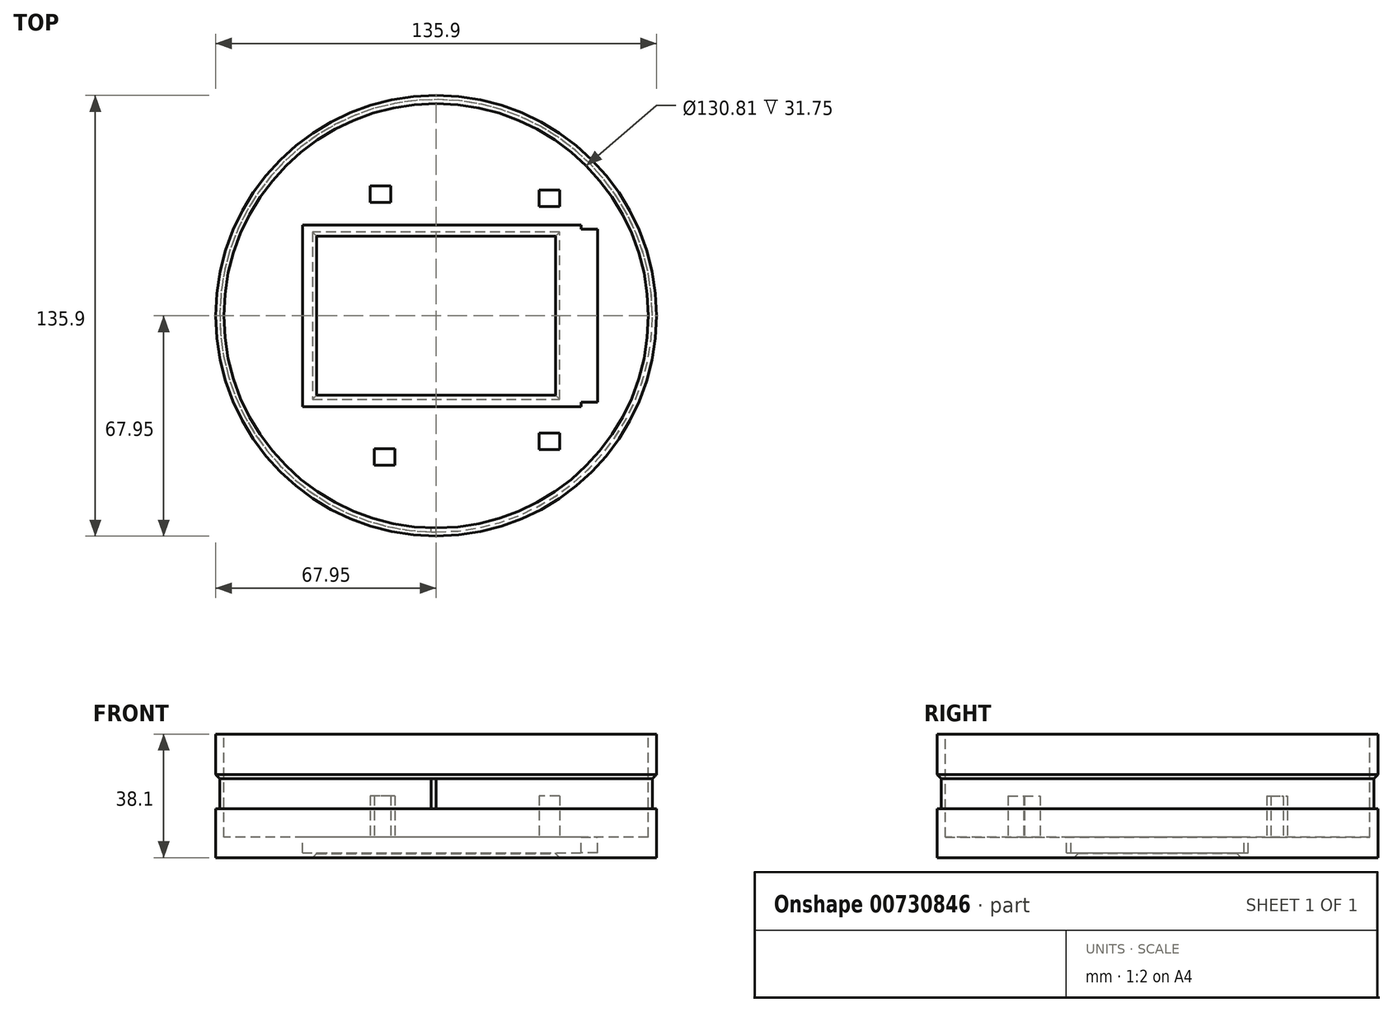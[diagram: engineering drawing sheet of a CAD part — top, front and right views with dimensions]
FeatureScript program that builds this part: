
annotation { "Feature Type Name" : "Feature", "Feature Type Description" : "" }
export const myFeature = defineFeature(function(context is Context, id is Id, definition is map)
    precondition{}
    {
        {
            var Q0;
            Q0=qCreatedBy(makeId("Top.planeOp"),FACE);
            var sketch = newSketch(context, id + "F0", { "sketchPlane" : qUnion([Q0])});
            skCircle(sketch, "E0", {"center": v(0, 0) * mm, "radius": 67.95 * mm});
            skSolve(sketch);
        }
        {
            var Q0;
            Q0 = qSketchRegion(id + "F0", true);
            extrude(context, id + "F1", {"entities" : qUnion([Q0]), "oppositeDirection" : true, "depth" : 38.1 * mm, "offsetDistance" : 25.4 * mm});
        }
        {
            var Q0;
            Q0=makeQuery(id+"F1.opExtrude","CAP_FACE",FACE,{"disambiguationData":[OSD([sQuery(id+"F0.wireOp",EDGE,"E0")])],"isStart":true});
            var sketch = newSketch(context, id + "F2", { "sketchPlane" : qUnion([Q0])});
            skCircle(sketch, "E1", {"center": v(0, 0) * mm, "radius": 65.4 * mm});
            skSolve(sketch);
        }
        {
            var Q0;
            Q0 = qSketchRegion(id + "F2", true);
            extrude(context, id + "F3", {"entities" : qUnion([Q0]), "operationType" : NewBodyOperationType.REMOVE, "oppositeDirection" : true, "depth" : 31.75 * mm, "offsetDistance" : 25.4 * mm});
        }
        {
            var Q0;
            Q0=makeQuery(id+"F1.opExtrude","CAP_FACE",FACE,{"disambiguationData":[OSD([sQuery(id+"F0.wireOp",EDGE,"E0")])],"isStart":true});
            cPlane(context, id + "F4", {"entities" : qUnion([Q0]), "cplaneType" : CPlaneType.OFFSET, "offset" : 19.05 * mm, "oppositeDirection" : true, "width" : 152.4 * mm, "height" : 152.4 * mm});
        }
        {
            var Q0;
            Q0=qCreatedBy(makeId("Front.planeOp"),FACE);
            var sketch = newSketch(context, id + "F5", { "sketchPlane" : qUnion([Q0])});
            skLineSegment(sketch, "E2.bottom", {"start": v(-66.68, -15.05) * mm, "end": v(-69.22, -15.05) * mm});
            skLineSegment(sketch, "E2.top", {"start": v(-66.68, -23.05) * mm, "end": v(-69.22, -23.05) * mm});
            skLineSegment(sketch, "E2.left", {"start": v(-66.68, -15.05) * mm, "end": v(-66.68, -23.05) * mm});
            skLineSegment(sketch, "E2.right", {"start": v(-69.22, -15.05) * mm, "end": v(-69.22, -23.05) * mm});
            skPoint(sketch, "E2.middle", {"position": v(-67.95, -19.05) * mm});
            skLineSegment(sketch, "E3", {"start": v(-67.95, -13.75) * mm, "end": v(-67.95, -24.76) * mm, "construction": true});
            skSolve(sketch);
        }
        {
            var Q0;
            Q0 = qSketchRegion(id + "F5", true);
            var Q1;
            Q1=makeQuery(id+"F1.opExtrude","SWEPT_FACE",FACE,{"disambiguationData":[OSD([sQuery(id+"F0.wireOp",EDGE,"E0")])]});
            revolve(context, id + "F6", {"operationType" : NewBodyOperationType.REMOVE, "surfaceOperationType" : NewSurfaceOperationType.NEW, "entities" : qUnion([Q0]), "axis" : qUnion([Q1]), "revolveType" : RevolveType.ONE_DIRECTION, "oppositeDirection" : true, "angle" : 360 * degree});
        }
        {
            var Q0;
            Q0=makeQuery(id+"F6.boolean.opBoolean","INTERSECT",EDGE,{"derivedFrom":[makeQuery(id+"F1.opExtrude","SWEPT_FACE",FACE,{"disambiguationData":[OSD([sQuery(id+"F0.wireOp",EDGE,"E0")])]}),makeQuery(id+"F6.opRevolve","SWEPT_FACE",FACE,{"disambiguationData":[OSD([sQuery(id+"F5.wireOp",EDGE,"E2.bottom")])]})]});
            chamfer(context, id + "F7", {"entities" : qUnion([Q0]), "width" : 2.54 * mm});
        }
        {
            var Q0;
            Q0=makeQuery(id+"F3.boolean.opBoolean","COPY",FACE,{"derivedFrom":makeQuery(id+"F3.opExtrude","CAP_FACE",FACE,{"disambiguationData":[OSD([sQuery(id+"F2.wireOp",EDGE,"E1")])],"isStart":false})});
            var sketch = newSketch(context, id + "F8", { "sketchPlane" : qUnion([Q0])});
            skLineSegment(sketch, "E4.bottom", {"start": v(36.83, 24.51) * mm, "end": v(-36.83, 24.51) * mm});
            skLineSegment(sketch, "E4.top", {"start": v(36.83, -24.51) * mm, "end": v(-36.83, -24.51) * mm});
            skLineSegment(sketch, "E4.left", {"start": v(36.83, 24.51) * mm, "end": v(36.83, -24.51) * mm});
            skLineSegment(sketch, "E4.right", {"start": v(-36.83, 24.51) * mm, "end": v(-36.83, -24.51) * mm});
            skPoint(sketch, "E4.middle", {"position": v(0, 0) * mm});
            skSolve(sketch);
        }
        {
            var Q0;
            Q0 = qSketchRegion(id + "F8", true);
            extrude(context, id + "F9", {"entities" : qUnion([Q0]), "operationType" : NewBodyOperationType.REMOVE, "endBound" : BoundingType.THROUGH_ALL, "oppositeDirection" : true, "depth" : 25.4 * mm, "offsetDistance" : 25.4 * mm});
        }
        {
            var Q0;
            Q0=makeQuery(id+"F3.boolean.opBoolean","COPY",FACE,{"derivedFrom":makeQuery(id+"F3.opExtrude","CAP_FACE",FACE,{"disambiguationData":[OSD([sQuery(id+"F2.wireOp",EDGE,"E1")])],"isStart":false})});
            var sketch = newSketch(context, id + "F10", { "sketchPlane" : qUnion([Q0])});
            skLineSegment(sketch, "E5", {"start": v(1.75, 4.14) * mm, "end": v(1.75, -15.67) * mm, "construction": true});
            skLineSegment(sketch, "E6", {"start": v(-9.6, 0) * mm, "end": v(14.27, 0) * mm, "construction": true});
            skLineSegment(sketch, "E7.bottom", {"start": v(44.68, 28) * mm, "end": v(-41.18, 28) * mm});
            skLineSegment(sketch, "E7.top", {"start": v(44.68, -28) * mm, "end": v(-41.18, -28) * mm});
            skLineSegment(sketch, "E7.left", {"start": v(44.68, 28) * mm, "end": v(44.68, -28) * mm});
            skLineSegment(sketch, "E7.right", {"start": v(-41.18, 28) * mm, "end": v(-41.18, -28) * mm});
            skPoint(sketch, "E7.middle", {"position": v(1.75, 0) * mm});
            skSolve(sketch);
        }
        {
            var Q0;
            Q0 = qSketchRegion(id + "F10", true);
            var Q1;
            Q1=makeQuery(id+"F1.opExtrude","CAP_FACE",FACE,{"disambiguationData":[OSD([sQuery(id+"F0.wireOp",EDGE,"E0")])],"isStart":false});
            extrude(context, id + "F11", {"entities" : qUnion([Q0]), "operationType" : NewBodyOperationType.REMOVE, "endBound" : BoundingType.UP_TO_SURFACE, "oppositeDirection" : true, "depth" : 25.4 * mm, "endBoundEntityFace" : qUnion([Q1]), "hasOffset" : true, "offsetDistance" : 1.52 * mm});
        }
        {
            var Q0;
            Q0=makeQuery(id+"F3.boolean.opBoolean","COPY",FACE,{"derivedFrom":makeQuery(id+"F3.opExtrude","CAP_FACE",FACE,{"disambiguationData":[OSD([sQuery(id+"F2.wireOp",EDGE,"E1")])],"isStart":false})});
            var sketch = newSketch(context, id + "F12", { "sketchPlane" : qUnion([Q0])});
            skLineSegment(sketch, "E8.bottom", {"start": v(44.68, 26.67) * mm, "end": v(49.76, 26.67) * mm});
            skLineSegment(sketch, "E8.top", {"start": v(44.68, -26.67) * mm, "end": v(49.76, -26.67) * mm});
            skLineSegment(sketch, "E8.left", {"start": v(44.68, 26.67) * mm, "end": v(44.68, -26.67) * mm});
            skLineSegment(sketch, "E8.right", {"start": v(49.76, 26.67) * mm, "end": v(49.76, -26.67) * mm});
            skSolve(sketch);
        }
        {
            var Q0;
            Q0 = qSketchRegion(id + "F12", true);
            var Q1;
            Q1=makeQuery(id+"F11.boolean.opBoolean","COPY",FACE,{"derivedFrom":makeQuery(id+"F11.opExtrude","CAP_FACE",FACE,{"disambiguationData":[OSD([sQuery(id+"F10.wireOp",EDGE,"E7.bottom"),sQuery(id+"F10.wireOp",EDGE,"E7.top"),sQuery(id+"F10.wireOp",EDGE,"E7.left"),sQuery(id+"F10.wireOp",EDGE,"E7.right")])],"isStart":false})});
            extrude(context, id + "F13", {"entities" : qUnion([Q0]), "operationType" : NewBodyOperationType.REMOVE, "endBound" : BoundingType.UP_TO_SURFACE, "oppositeDirection" : true, "depth" : 3.8 * mm, "endBoundEntityFace" : qUnion([Q1]), "offsetDistance" : 25.4 * mm});
        }
        {
            var Q0;
            Q0=makeQuery(id+"F9.boolean.opBoolean","INTERSECT",EDGE,{"derivedFrom":[makeQuery(id+"F1.opExtrude","CAP_FACE",FACE,{"disambiguationData":[OSD([sQuery(id+"F0.wireOp",EDGE,"E0")])],"isStart":false}),makeQuery(id+"F9.opExtrude","SWEPT_FACE",FACE,{"disambiguationData":[OSD([sQuery(id+"F8.wireOp",EDGE,"E4.bottom")])]})]});
            var Q1;
            Q1=makeQuery(id+"F9.boolean.opBoolean","INTERSECT",EDGE,{"derivedFrom":[makeQuery(id+"F1.opExtrude","CAP_FACE",FACE,{"disambiguationData":[OSD([sQuery(id+"F0.wireOp",EDGE,"E0")])],"isStart":false}),makeQuery(id+"F9.opExtrude","SWEPT_FACE",FACE,{"disambiguationData":[OSD([sQuery(id+"F8.wireOp",EDGE,"E4.right")])]})]});
            var Q2;
            Q2=makeQuery(id+"F9.boolean.opBoolean","INTERSECT",EDGE,{"derivedFrom":[makeQuery(id+"F1.opExtrude","CAP_FACE",FACE,{"disambiguationData":[OSD([sQuery(id+"F0.wireOp",EDGE,"E0")])],"isStart":false}),makeQuery(id+"F9.opExtrude","SWEPT_FACE",FACE,{"disambiguationData":[OSD([sQuery(id+"F8.wireOp",EDGE,"E4.left")])]})]});
            var Q3;
            Q3=makeQuery(id+"F9.boolean.opBoolean","INTERSECT",EDGE,{"derivedFrom":[makeQuery(id+"F1.opExtrude","CAP_FACE",FACE,{"disambiguationData":[OSD([sQuery(id+"F0.wireOp",EDGE,"E0")])],"isStart":false}),makeQuery(id+"F9.opExtrude","SWEPT_FACE",FACE,{"disambiguationData":[OSD([sQuery(id+"F8.wireOp",EDGE,"E4.top")])]})]});
            chamfer(context, id + "F14", {"entities" : qUnion([Q0, Q1, Q2, Q3]), "width" : 1.27 * mm});
        }
        {
            var Q0;
            Q0=qCreatedBy(makeId("Front.planeOp"),FACE);
            var sketch = newSketch(context, id + "F15", { "sketchPlane" : qUnion([Q0])});
            skLineSegment(sketch, "E9.bottom", {"start": v(0, -13.78) * mm, "end": v(-1.52, -13.78) * mm});
            skLineSegment(sketch, "E9.top", {"start": v(0, -23.05) * mm, "end": v(-1.52, -23.05) * mm});
            skLineSegment(sketch, "E9.left", {"start": v(0, -13.78) * mm, "end": v(0, -23.05) * mm});
            skLineSegment(sketch, "E9.right", {"start": v(-1.52, -13.78) * mm, "end": v(-1.52, -23.05) * mm});
            skSolve(sketch);
        }
        {
            var Q0;
            Q0 = qSketchRegion(id + "F15", true);
            extrude(context, id + "F16", {"entities" : qUnion([Q0]), "operationType" : NewBodyOperationType.REMOVE, "endBound" : BoundingType.THROUGH_ALL, "depth" : 25.4 * mm, "offsetDistance" : 25.4 * mm});
        }
        {
            var Q0;
            Q0=makeQuery(id+"F3.boolean.opBoolean","COPY",FACE,{"derivedFrom":makeQuery(id+"F3.opExtrude","CAP_FACE",FACE,{"disambiguationData":[OSD([sQuery(id+"F2.wireOp",EDGE,"E1")])],"isStart":false})});
            var sketch = newSketch(context, id + "F17", { "sketchPlane" : qUnion([Q0])});
            skLineSegment(sketch, "E10", {"start": v(0, 24.43) * mm, "end": v(0, -33.61) * mm, "construction": true});
            skLineSegment(sketch, "E11.bottom", {"start": v(36.2, -51.44) * mm, "end": v(-18.41, -51.44) * mm, "construction": true});
            skLineSegment(sketch, "E11.top", {"start": v(36.2, 51.44) * mm, "end": v(-18.41, 51.44) * mm, "construction": true});
            skLineSegment(sketch, "E11.left", {"start": v(36.2, -51.43) * mm, "end": v(36.2, 51.44) * mm, "construction": true});
            skLineSegment(sketch, "E11.right", {"start": v(-18.41, -51.44) * mm, "end": v(-18.41, 51.44) * mm, "construction": true});
            skPoint(sketch, "E11.middle", {"position": v(8.9, 0) * mm});
            skLineSegment(sketch, "E12", {"start": v(-9.63, 0) * mm, "end": v(23.44, 0) * mm, "construction": true});
            skLineSegment(sketch, "E13.bottom", {"start": v(-13.97, 34.92) * mm, "end": v(-20.32, 34.92) * mm});
            skLineSegment(sketch, "E13.top", {"start": v(-13.97, 40) * mm, "end": v(-20.32, 40) * mm});
            skLineSegment(sketch, "E13.left", {"start": v(-13.97, 34.92) * mm, "end": v(-13.97, 40) * mm});
            skLineSegment(sketch, "E13.right", {"start": v(-20.32, 34.92) * mm, "end": v(-20.32, 40) * mm});
            skPoint(sketch, "E13.middle", {"position": v(-17.14, 37.46) * mm});
            skLineSegment(sketch, "E14.bottom", {"start": v(38.1, 33.66) * mm, "end": v(31.75, 33.66) * mm});
            skLineSegment(sketch, "E14.top", {"start": v(38.1, 38.74) * mm, "end": v(31.75, 38.74) * mm});
            skLineSegment(sketch, "E14.left", {"start": v(38.1, 33.66) * mm, "end": v(38.1, 38.74) * mm});
            skLineSegment(sketch, "E14.right", {"start": v(31.75, 33.66) * mm, "end": v(31.75, 38.74) * mm});
            skPoint(sketch, "E14.middle", {"position": v(34.93, 36.2) * mm});
            skLineSegment(sketch, "E15.bottom", {"start": v(-12.7, -46.05) * mm, "end": v(-19.05, -46.05) * mm});
            skLineSegment(sketch, "E15.top", {"start": v(-12.7, -40.97) * mm, "end": v(-19.05, -40.97) * mm});
            skLineSegment(sketch, "E15.left", {"start": v(-12.7, -46.05) * mm, "end": v(-12.7, -40.97) * mm});
            skLineSegment(sketch, "E15.right", {"start": v(-19.05, -46.05) * mm, "end": v(-19.05, -40.97) * mm});
            skPoint(sketch, "E15.middle", {"position": v(-15.87, -43.5) * mm});
            skLineSegment(sketch, "E16.bottom", {"start": v(38.1, -41.27) * mm, "end": v(31.75, -41.27) * mm});
            skLineSegment(sketch, "E16.top", {"start": v(38.1, -36.2) * mm, "end": v(31.75, -36.2) * mm});
            skLineSegment(sketch, "E16.left", {"start": v(38.1, -41.27) * mm, "end": v(38.1, -36.2) * mm});
            skLineSegment(sketch, "E16.right", {"start": v(31.75, -41.27) * mm, "end": v(31.75, -36.2) * mm});
            skPoint(sketch, "E16.middle", {"position": v(34.92, -38.73) * mm});
            skLineSegment(sketch, "E17.bottom", {"start": v(26.67, 51.43) * mm, "end": v(14.73, 51.43) * mm, "construction": true});
            skLineSegment(sketch, "E17.top", {"start": v(26.67, 57.53) * mm, "end": v(14.73, 57.53) * mm, "construction": true});
            skLineSegment(sketch, "E17.left", {"start": v(26.67, 51.43) * mm, "end": v(26.67, 57.53) * mm, "construction": true});
            skLineSegment(sketch, "E17.right", {"start": v(14.73, 51.43) * mm, "end": v(14.73, 57.53) * mm, "construction": true});
            skPoint(sketch, "E17.middle", {"position": v(20.7, 54.48) * mm});
            skSolve(sketch);
        }
        {
            var Q0;
            Q0 = qSketchRegion(id + "F17", true);
            extrude(context, id + "F18", {"entities" : qUnion([Q0]), "operationType" : NewBodyOperationType.ADD, "depth" : 12.7 * mm, "offsetDistance" : 25.4 * mm});
        }
    });
